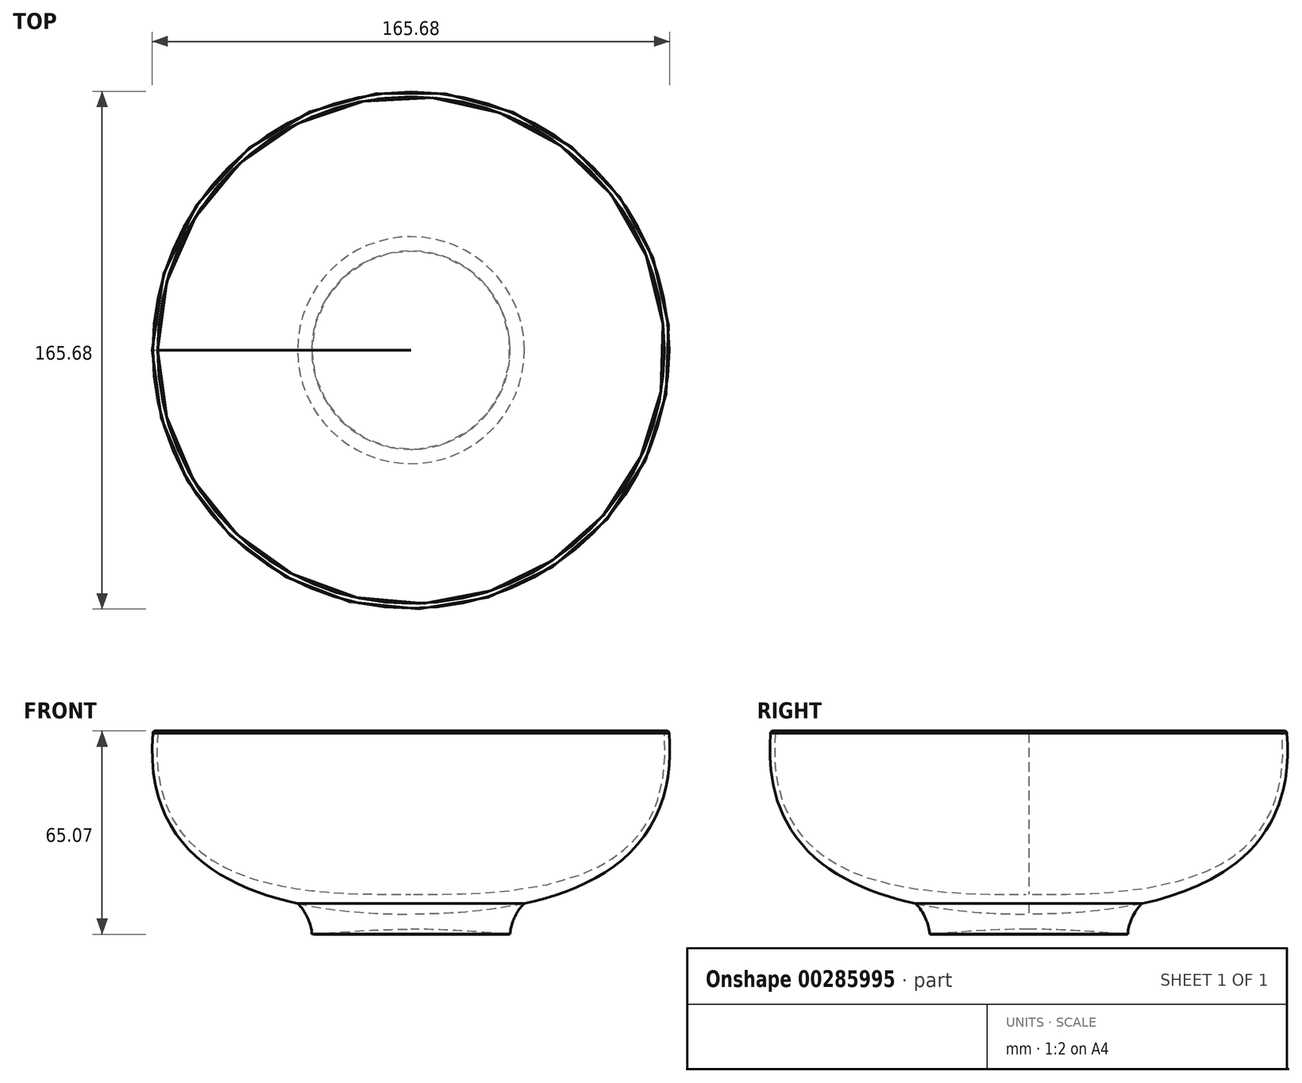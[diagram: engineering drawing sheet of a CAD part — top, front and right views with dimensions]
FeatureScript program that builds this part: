
annotation { "Feature Type Name" : "Feature", "Feature Type Description" : "" }
export const myFeature = defineFeature(function(context is Context, id is Id, definition is map)
    precondition{}
    {
        {
            var Q0;
            Q0=qCreatedBy(makeId("Front.planeOp"),FACE);
            var sketch = newSketch(context, id + "F0", { "sketchPlane" : qUnion([Q0])});
            skLineSegment(sketch, "E0", {"start": v(0, -109.83) * mm, "end": v(0, 159.5) * mm, "construction": true});
            skFitSpline(sketch, "E1", {"points": [v(-82.55, 31.97) * mm, v(0, -26.7) * mm], "startDerivative": vector(-14.68, -162) * mm, "endDerivative": vector(88.52, -0.62) * mm});
            skFitSpline(sketch, "E2.MirrorCS", {"points": [v(82.55, 31.97) * mm, v(0, -26.7) * mm], "startDerivative": vector(14.68, -162) * mm, "endDerivative": vector(-88.52, -0.62) * mm});
            skLineSegment(sketch, "E3", {"start": v(-82.55, 31.97) * mm, "end": v(82.55, 31.97) * mm});
            skFitSpline(sketch, "E4", {"points": [v(-36.31, -23.25) * mm, v(-31.75, -33.06) * mm], "startDerivative": vector(6.65, -5.25) * mm, "endDerivative": vector(-0.26, -9.03) * mm});
            skFitSpline(sketch, "E5.MirrorCS", {"points": [v(36.31, -23.25) * mm, v(31.75, -33.06) * mm], "startDerivative": vector(-6.65, -5.25) * mm, "endDerivative": vector(0.26, -9.03) * mm});
            skFitSpline(sketch, "E6", {"points": [v(-31.75, -33.06) * mm, v(-30.16, -33.06) * mm, v(0, -31.47) * mm, v(30.16, -33.06) * mm, v(31.75, -33.06) * mm], "startDerivative": vector(18.87, -2) * mm, "endDerivative": vector(19.1, 2.02) * mm});
            skFitSpline(sketch, "E7", {"points": [v(-81.03, 31.97) * mm, v(0, -20.36) * mm], "startDerivative": vector(-14.68, -162) * mm, "endDerivative": vector(88.52, -0.62) * mm});
            skFitSpline(sketch, "E8.MirrorCS", {"points": [v(81.03, 31.97) * mm, v(0, -20.36) * mm], "startDerivative": vector(14.68, -162) * mm, "endDerivative": vector(-88.52, -0.62) * mm});
            skLineSegment(sketch, "E9", {"start": v(0, -43.46) * mm, "end": v(0, 79.19) * mm});
            skSolve(sketch);
        }
        {
            var Q0;
            {var subQ0=sQuery(id+"F0.wireOp",EDGE,"E7");Q0=makeQuery(id+"F0.imprint","IMPRINT",FACE,{"disambiguationData":[TD([[makeQuery(id+"F0.imprint","IMPRINT",EDGE,{"derivedFrom":subQ0}),-1.0]])]});}
            var Q1;
            Q1=sQuery(id+"F0.wireOp",EDGE,"E9");
            revolve(context, id + "F1", {"entities" : qUnion([Q0]), "axis" : qUnion([Q1]), "revolveType" : RevolveType.FULL});
        }
        {
            var Q0;
            Q0=makeQuery(id+"F1.opRevolve","SWEPT_EDGE",EDGE,{"disambiguationData":[OSD([sQuery(id+"F0.wireOp",EDGE,"E1"),sQuery(id+"F0.wireOp",EDGE,"E3")])]});
            var Q1;
            Q1=makeQuery(id+"F1.opRevolve","SWEPT_EDGE",EDGE,{"disambiguationData":[OSD([sQuery(id+"F0.wireOp",EDGE,"E3"),sQuery(id+"F0.wireOp",EDGE,"E7")])]});
            fillet(context, id + "F2", {"entities" : qUnion([Q0, Q1]), "radius" : 0.74 * mm, "tangentPropagation" : true, "allowEdgeOverflow" : false});
        }
        {
            var Q0;
            {var subQ3=sQuery(id+"F0.wireOp",EDGE,"E4");Q0=makeQuery(id+"F0.imprint","IMPRINT",FACE,{"disambiguationData":[TD([[makeQuery(id+"F0.imprint","IMPRINT",EDGE,{"derivedFrom":subQ3}),1.0]])]});}
            var Q1;
            Q1=sQuery(id+"F0.wireOp",EDGE,"E9");
            revolve(context, id + "F3", {"entities" : qUnion([Q0]), "axis" : qUnion([Q1]), "revolveType" : RevolveType.FULL});
        }
    });
